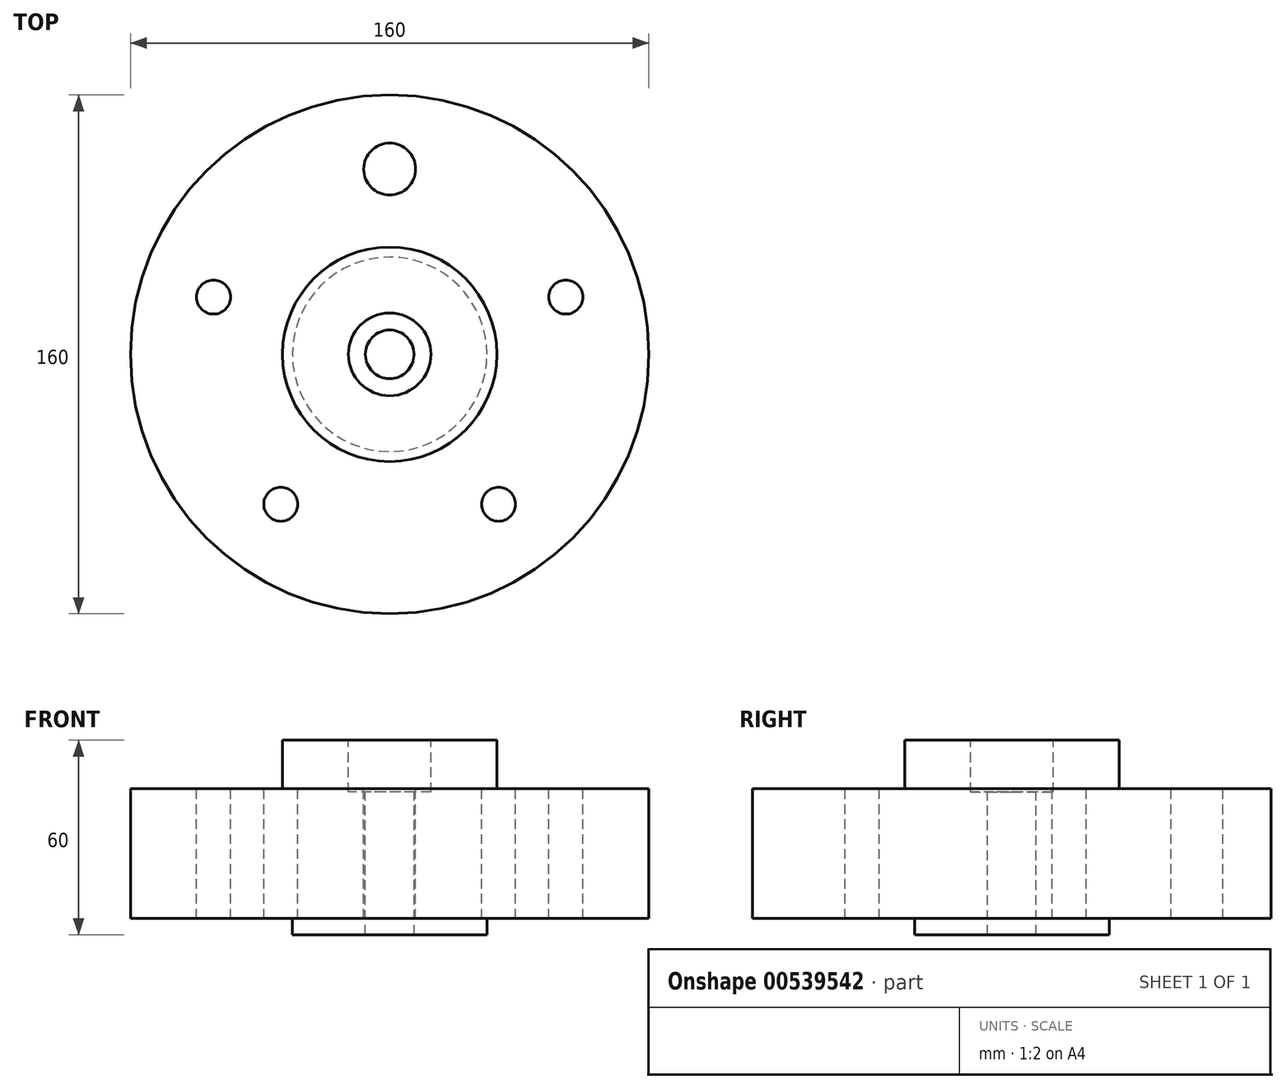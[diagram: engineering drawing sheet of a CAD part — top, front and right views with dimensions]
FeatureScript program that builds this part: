
annotation { "Feature Type Name" : "Feature", "Feature Type Description" : "" }
export const myFeature = defineFeature(function(context is Context, id is Id, definition is map)
    precondition{}
    {
        {
            var Q0;
            Q0=qCreatedBy(makeId("Front.planeOp"),FACE);
            var sketch = newSketch(context, id + "F0", { "sketchPlane" : qUnion([Q0])});
            skLineSegment(sketch, "E0.bottom", {"start": v(30, 0) * mm, "end": v(80, 0) * mm});
            skLineSegment(sketch, "E0.top", {"start": v(33.08, 40) * mm, "end": v(80, 40) * mm});
            skLineSegment(sketch, "E0.right", {"start": v(80, 0) * mm, "end": v(80, 40) * mm});
            skPoint(sketch, "E1.oppositeSnap0", {"position": v(33.08, 40) * mm});
            skLineSegment(sketch, "E1.top", {"start": v(0, 55) * mm, "end": v(33.08, 55) * mm});
            skLineSegment(sketch, "E1.right", {"start": v(33.08, 40) * mm, "end": v(33.08, 55) * mm});
            skPoint(sketch, "E0.left.end.orphan", {"position": v(-13.85, 40) * mm});
            skLineSegment(sketch, "E2", {"start": v(0, 55) * mm, "end": v(0, 0) * mm});
            skLineSegment(sketch, "E3.top", {"start": v(0, -5) * mm, "end": v(30, -5) * mm});
            skLineSegment(sketch, "E3.left", {"start": v(0, 0) * mm, "end": v(0, -5) * mm});
            skLineSegment(sketch, "E3.right", {"start": v(30, 0) * mm, "end": v(30, -5) * mm});
            skSolve(sketch);
        }
        {
            var Q0;
            Q0=makeQuery(id+"F0.imprint","IMPRINT",FACE,{"disambiguationData":[TD([[makeQuery(id+"F0.imprint","IMPRINT",EDGE,{"derivedFrom":sQuery(id+"F0.wireOp",EDGE,"E0.bottom")}),1.0]])]});
            var Q1;
            Q1=sQuery(id+"F0.wireOp",EDGE,"E2");
            revolve(context, id + "F1", {"entities" : qUnion([Q0]), "axis" : qUnion([Q1]), "revolveType" : RevolveType.FULL});
        }
        {
            var Q0;
            Q0=makeQuery(id+"F1.opRevolve","SWEPT_FACE",FACE,{"disambiguationData":[OSD([sQuery(id+"F0.wireOp",EDGE,"E0.top")])]});
            var sketch = newSketch(context, id + "F2", { "sketchPlane" : qUnion([Q0])});
            skCircle(sketch, "E4", {"center": v(0, 0) * mm, "radius": 57.15 * mm});
            skPoint(sketch, "E5", {"position": v(0, 57.15) * mm});
            skPoint(sketch, "E6.1.0", {"position": v(-54.35, 17.66) * mm});
            skPoint(sketch, "E6.2.0", {"position": v(-33.6, -46.24) * mm});
            skPoint(sketch, "E6.3.0", {"position": v(33.6, -46.24) * mm});
            skPoint(sketch, "E6.4.0", {"position": v(54.35, 17.66) * mm});
            skSolve(sketch);
        }
        {
            var Q0;
            Q0=makeQuery(id+"F1.opRevolve","SWEPT_FACE",FACE,{"disambiguationData":[OSD([sQuery(id+"F0.wireOp",EDGE,"E1.top")])]});
            var sketch = newSketch(context, id + "F3", { "sketchPlane" : qUnion([Q0])});
            skPoint(sketch, "E7", {"position": v(0, 0) * mm});
            skCircle(sketch, "E8", {"center": v(0, 0) * mm, "radius": 20 * mm});
            skPoint(sketch, "E9", {"position": v(0, 20) * mm});
            skCircle(sketch, "E10", {"center": v(0, 0) * mm, "radius": 26 * mm});
            skSolve(sketch);
        }
        {
            var Q0;
            Q0=sQuery(id+"F3.wireOp",VERTEX,"E7");
            var Q1;
            Q1=makeQuery(id+"F1.opRevolve","SWEPT_BODY",BODY,{"disambiguationData":[OSD([sQuery(id+"F0.wireOp",EDGE,"E0.bottom"),sQuery(id+"F0.wireOp",EDGE,"E0.top"),sQuery(id+"F0.wireOp",EDGE,"E0.right"),sQuery(id+"F0.wireOp",EDGE,"E1.top"),sQuery(id+"F0.wireOp",EDGE,"E1.right"),sQuery(id+"F0.wireOp",EDGE,"E2")])]});
            hole(context, id + "F4", {"style" : HoleStyle.C_BORE, "endStyle" : HoleEndStyle.THROUGH, "standardTappedOrClearance" : lookupTablePath({ "standard" : "ISO", "size" : "15", "type" : "Drilled" }), "standardBlindInLast" : lookupTablePath({ "standard" : "ISO", "size" : "15", "type" : "Drilled" }), "holeDiameter" : 15 * mm, "cBoreDiameter" : 25.5 * mm, "cBoreDepth" : 16 * mm, "tappedDepth" : 1 * mm, "tapClearance" : 3, "locations" : qUnion([Q0]), "scope" : qUnion([Q1])});
        }
        {
            var Q0;
            Q0=sQuery(id+"F2.wireOp",VERTEX,"E6.1.0");
            var Q1;
            Q1=sQuery(id+"F2.wireOp",VERTEX,"E6.2.0");
            var Q2;
            Q2=sQuery(id+"F2.wireOp",VERTEX,"E6.3.0");
            var Q3;
            Q3=sQuery(id+"F2.wireOp",VERTEX,"E6.4.0");
            var Q4;
            Q4=makeQuery(id+"F1.opRevolve","SWEPT_BODY",BODY,{"disambiguationData":[OSD([sQuery(id+"F0.wireOp",EDGE,"E0.bottom"),sQuery(id+"F0.wireOp",EDGE,"E0.top"),sQuery(id+"F0.wireOp",EDGE,"E0.right"),sQuery(id+"F0.wireOp",EDGE,"E1.top"),sQuery(id+"F0.wireOp",EDGE,"E1.right"),sQuery(id+"F0.wireOp",EDGE,"E2"),sQuery(id+"F0.wireOp",EDGE,"E3.top"),sQuery(id+"F0.wireOp",EDGE,"E3.left"),sQuery(id+"F0.wireOp",EDGE,"E3.right")])]});
            hole(context, id + "F5", {"style" : HoleStyle.SIMPLE, "endStyle" : HoleEndStyle.THROUGH, "standardTappedOrClearance" : lookupTablePath({ "standard" : "ISO", "engagement" : "75%", "pitch" : "1.5 mm", "size" : "M12", "type" : "Tapped" }), "standardBlindInLast" : lookupTablePath({ "standard" : "ISO", "engagement" : "75%", "pitch" : "1.5 mm", "size" : "M12", "type" : "Tapped" }), "holeDiameter" : 10.5 * mm, "majorDiameter" : 12 * mm, "showTappedDepth" : true, "tappedDepth" : 20 * mm, "tapClearance" : 3, "locations" : qUnion([Q0, Q1, Q2, Q3]), "scope" : qUnion([Q4])});
        }
        {
            var Q0;
            Q0=sQuery(id+"F2.wireOp",VERTEX,"E5");
            var Q1;
            Q1=makeQuery(id+"F1.opRevolve","SWEPT_BODY",BODY,{"disambiguationData":[OSD([sQuery(id+"F0.wireOp",EDGE,"E0.bottom"),sQuery(id+"F0.wireOp",EDGE,"E0.top"),sQuery(id+"F0.wireOp",EDGE,"E0.right"),sQuery(id+"F0.wireOp",EDGE,"E1.top"),sQuery(id+"F0.wireOp",EDGE,"E1.right"),sQuery(id+"F0.wireOp",EDGE,"E2"),sQuery(id+"F0.wireOp",EDGE,"E3.top"),sQuery(id+"F0.wireOp",EDGE,"E3.left"),sQuery(id+"F0.wireOp",EDGE,"E3.right")])]});
            hole(context, id + "F6", {"style" : HoleStyle.SIMPLE, "endStyle" : HoleEndStyle.THROUGH, "standardTappedOrClearance" : lookupTablePath({ "standard" : "ISO", "size" : "16", "type" : "Drilled" }), "standardBlindInLast" : lookupTablePath({ "standard" : "ISO", "size" : "16", "type" : "Drilled" }), "holeDiameter" : 16 * mm, "majorDiameter" : 12 * mm, "tappedDepth" : 20 * mm, "tapClearance" : 3, "locations" : qUnion([Q0]), "scope" : qUnion([Q1])});
        }
    });
